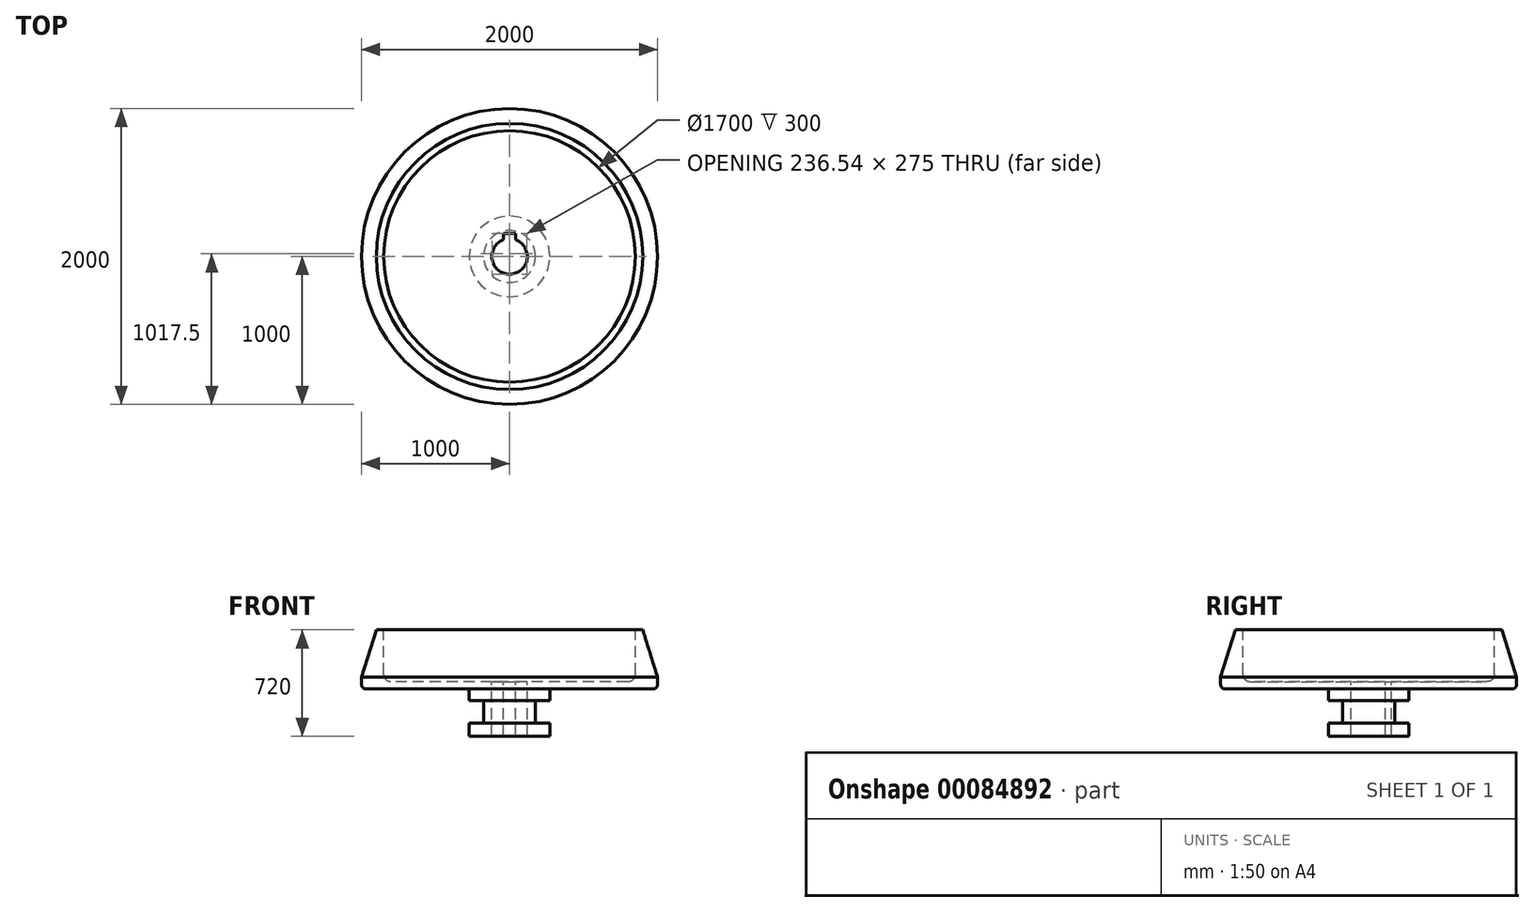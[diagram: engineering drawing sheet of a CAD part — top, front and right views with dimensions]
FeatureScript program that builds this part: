
annotation { "Feature Type Name" : "Feature", "Feature Type Description" : "" }
export const myFeature = defineFeature(function(context is Context, id is Id, definition is map)
    precondition{}
    {
        {
            var Q0;
            Q0=qCreatedBy(makeId("Front.planeOp"),FACE);
            var sketch = newSketch(context, id + "F0", { "sketchPlane" : qUnion([Q0])});
            skLineSegment(sketch, "E0", {"start": v(0, 466.45) * mm, "end": v(0, -511.77) * mm, "construction": true});
            skLineSegment(sketch, "E1", {"start": v(120, 0) * mm, "end": v(120, 370) * mm});
            skLineSegment(sketch, "E2", {"start": v(120, 0) * mm, "end": v(272.54, 0) * mm});
            skLineSegment(sketch, "E3", {"start": v(272.54, 0) * mm, "end": v(272.54, 90) * mm});
            skLineSegment(sketch, "E4", {"start": v(272.54, 90) * mm, "end": v(175.26, 90) * mm});
            skLineSegment(sketch, "E5", {"start": v(175.26, 90) * mm, "end": v(175.26, 240) * mm});
            skLineSegment(sketch, "E6", {"start": v(175.26, 240) * mm, "end": v(272.54, 240) * mm});
            skLineSegment(sketch, "E7", {"start": v(272.54, 240) * mm, "end": v(272.54, 320) * mm});
            skLineSegment(sketch, "E8", {"start": v(272.54, 320) * mm, "end": v(970, 320) * mm});
            skLineSegment(sketch, "E9", {"start": v(1000, 400) * mm, "end": v(900, 720) * mm});
            skLineSegment(sketch, "E10", {"start": v(900, 720) * mm, "end": v(850, 720) * mm});
            skLineSegment(sketch, "E11", {"start": v(850, 720) * mm, "end": v(850, 420) * mm});
            skLineSegment(sketch, "E12", {"start": v(800, 370) * mm, "end": v(120, 370) * mm});
            skPoint(sketch, "E13.visualSharp", {"position": v(850, 370) * mm});
            skArc(sketch, "E13.filletArc", {"start": v(800, 370) * mm, "mid": v(835.36, 384.64) * mm, "end": v(850, 420) * mm});
            skLineSegment(sketch, "E14", {"start": v(1000, 400) * mm, "end": v(1000, 350) * mm});
            skPoint(sketch, "E15.visualSharp", {"position": v(1000, 320) * mm});
            skArc(sketch, "E15.filletArc", {"start": v(970, 320) * mm, "mid": v(991.21, 328.79) * mm, "end": v(1000, 350) * mm});
            skSolve(sketch);
        }
        {
            var Q0;
            Q0 = qSketchRegion(id + "F0", true);
            var Q1;
            Q1=sQuery(id+"F0.wireOp",EDGE,"E0");
            revolve(context, id + "F1", {"entities" : qUnion([Q0]), "axis" : qUnion([Q1]), "revolveType" : RevolveType.FULL});
        }
        {
            var Q0;
            Q0=makeQuery(id+"F1.opRevolve","SWEPT_FACE",FACE,{"disambiguationData":[OSD([sQuery(id+"F0.wireOp",EDGE,"E12")])]});
            var sketch = newSketch(context, id + "F2", { "sketchPlane" : qUnion([Q0])});
            skPoint(sketch, "E16", {"position": v(0, 120) * mm});
            skLineSegment(sketch, "E17.bottom", {"start": v(-40, 85) * mm, "end": v(40, 85) * mm});
            skLineSegment(sketch, "E17.top", {"start": v(-40, 155) * mm, "end": v(40, 155) * mm});
            skLineSegment(sketch, "E17.left", {"start": v(-40, 85) * mm, "end": v(-40, 155) * mm});
            skLineSegment(sketch, "E17.right", {"start": v(40, 85) * mm, "end": v(40, 155) * mm});
            skSolve(sketch);
        }
        {
            var Q0;
            Q0 = qSketchRegion(id + "F2", true);
            extrude(context, id + "F3", {"entities" : qUnion([Q0]), "operationType" : NewBodyOperationType.REMOVE, "endBound" : BoundingType.THROUGH_ALL, "oppositeDirection" : true, "depth" : 25 * mm});
        }
    });
